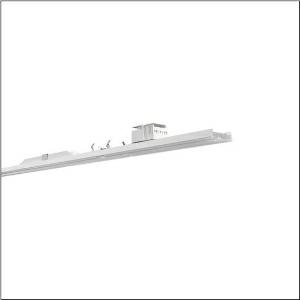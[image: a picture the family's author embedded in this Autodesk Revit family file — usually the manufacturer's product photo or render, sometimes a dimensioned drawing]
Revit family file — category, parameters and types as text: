
# Revit family: licross_r__11_recessed_mo_51tl18vn48xf_494e
name_source: partatom
category: Lighting Fixtures
units: mm (PartAtom-declared; Revit-internal decimal feet)

## family parameters
Cut with Voids When Loaded = No
Host = Face
Light Source = No
Part Type = Normal
Room Calculation Point = No
Round Connector Dimension = Use Diameter
Shared = No

## types (1)
- --- (1 x LED, 8020 lm, 49.4 W, 4000K)
    Apparent Load = 49 VA
    CIE Flux Codes = 83 96 99 100 100
    Color Rendering = 80
    Color Temperature = 4000K
    Default Elevation = 1800 mm
    Description = Licross® 11 Recessed MOluminaire insert, length: 1.500mm, width: 66mm, height: 67mm, LED rated luminous flux: 8.020lm, light colour: 840, control gear: DALI 2, CLO, control gear: ECG DALI, with plug, 5-pole, with phase selection, mains connection: 220..240V, AC, 50/60Hz, halogen-free wiring, primary optical cover: cover, of PMMA, light emission: direct distribution, protection rating (complete): IP40, insulation class (complete): insulation class I (protective earthing), certification: CE, ENEC, VDE, UKCA, protection symbol: D if used in an environment without relevant dust loads with corresponding accessories, permissible ambient temperature for indoor applications: -25..+35°C, corresponds to IFS (International Featured Standards) requirements for safety and quality in the food industry, reducing of maximum allowable ambient temperature of 5°C with ceiling mounting, packaging unit: 1 piece
    Height = 58 mm
    Lamp = 1 x LED
    Lamp Light Flux = 8020 lm
    Lamp Power = 49.4 W
    Lamp count = 1
    Length = 1500 mm
    Luminous efficacy = 162 lm/W
    Manufacturer = Siteco
    ModVariant = No
    Model = 51TL18VN48XF
    Mounting Place = Ceiling
    Mounting Type = Pendant
    Number of Poles = 1
    OnlyDefault = Yes
    Power Factor = 1
    Product Name = Licross® 11 Recessed MO
    Product group = luminaire insert
    ProductGroupID = 902
    Protection Class = Protection class I
    Protection Degree = IP 40
    RLX_Detail_Level = 1
    RlxData = <blob elided: 22349 chars, md5=89420b71>
    Socket = socket
    Standby Power = 0 W
    System Light Flux = 8020 lm
    System Power = 49 W
    Type Comments = factory setting: luminous flux: 100 % | dim-lin: 254 | 325 mA
    Type Image = l_1266722.jpg
    URL = http://relux.com
    VarID = @adj_129113
    Voltage = 0 V
    Weight = 0.00 kg
    Width = 66 mm

## geometry (parser evidence)
native form markers: Blend x4, Sweep x13
no freeform markers — native parametric forms only
